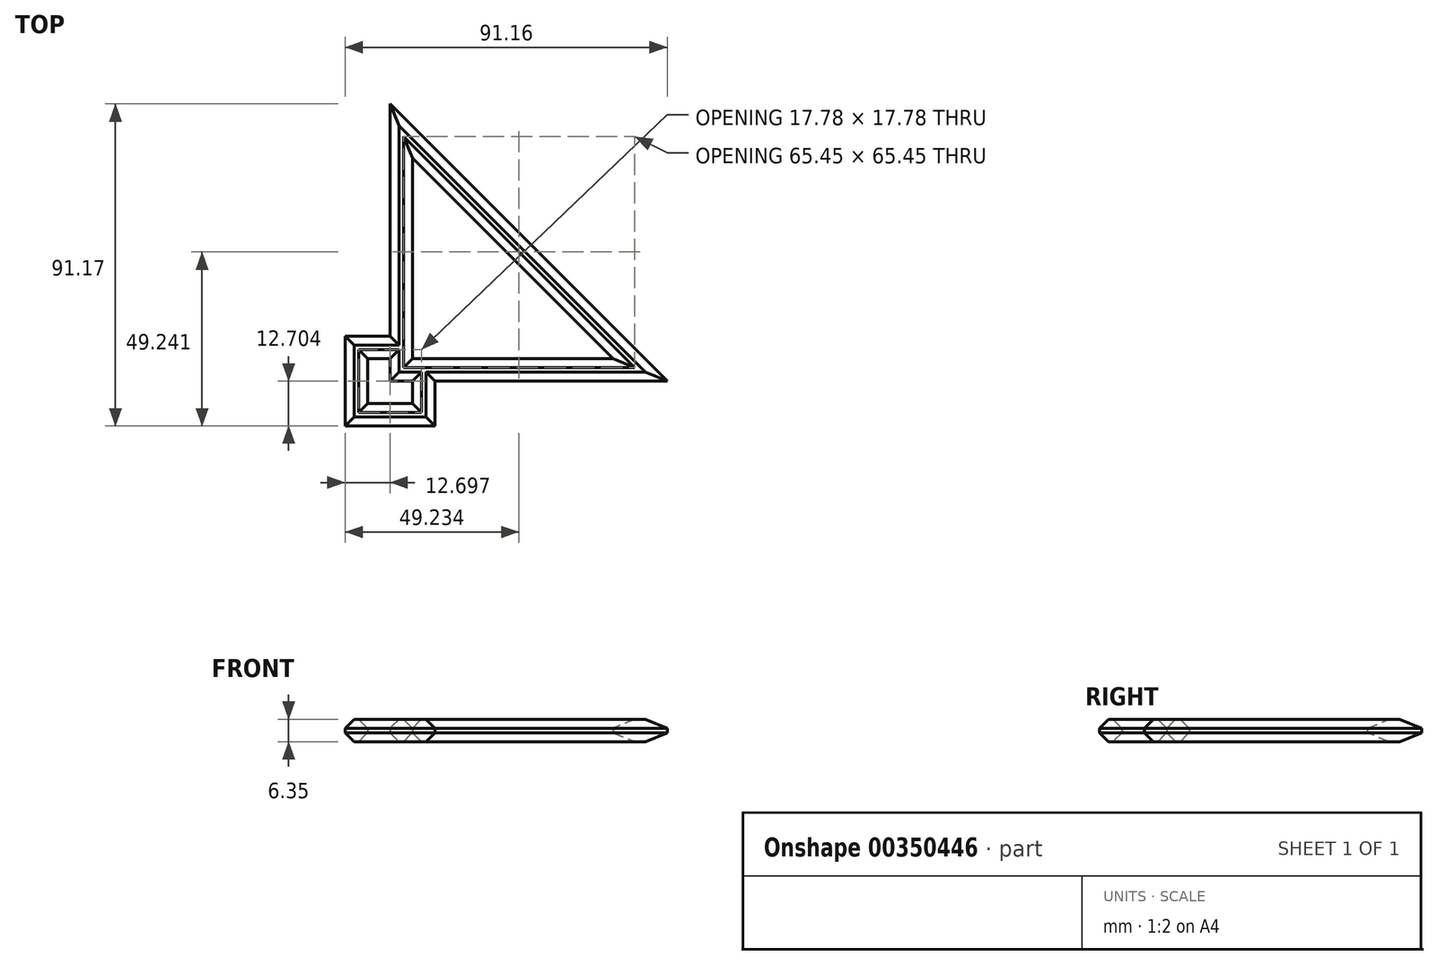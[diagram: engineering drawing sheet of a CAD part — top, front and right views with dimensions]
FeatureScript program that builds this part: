
annotation { "Feature Type Name" : "Feature", "Feature Type Description" : "" }
export const myFeature = defineFeature(function(context is Context, id is Id, definition is map)
    precondition{}
    {
        {
            var Q0;
            Q0=qCreatedBy(makeId("Top.planeOp"),FACE);
            var sketch = newSketch(context, id + "F0", { "sketchPlane" : qUnion([Q0])});
            skLineSegment(sketch, "E0", {"start": v(62.73, -3.4) * mm, "end": v(62.73, 2.94) * mm});
            skLineSegment(sketch, "E1", {"start": v(62.73, 2.94) * mm, "end": v(-3.03, 2.94) * mm});
            skLineSegment(sketch, "E2", {"start": v(-3.03, -0.37) * mm, "end": v(-3.03, 68.7) * mm});
            skLineSegment(sketch, "E3", {"start": v(-3.03, 68.7) * mm, "end": v(-9.38, 68.7) * mm});
            skLineSegment(sketch, "E4", {"start": v(-3.03, 68.7) * mm, "end": v(62.73, 2.94) * mm});
            skLineSegment(sketch, "E5", {"start": v(-3.03, 59.73) * mm, "end": v(53.75, 2.94) * mm});
            skLineSegment(sketch, "E6", {"start": v(-9.38, 68.7) * mm, "end": v(-9.38, 72.28) * mm});
            skLineSegment(sketch, "E7", {"start": v(-3.03, 68.7) * mm, "end": v(-9.38, 75.06) * mm});
            skLineSegment(sketch, "E8", {"start": v(62.73, 2.94) * mm, "end": v(69.08, -3.4) * mm});
            skLineSegment(sketch, "E9", {"start": v(-9.38, 72.28) * mm, "end": v(-9.38, 75.06) * mm});
            skLineSegment(sketch, "E10", {"start": v(-9.38, 9.3) * mm, "end": v(-22.08, 9.3) * mm});
            skLineSegment(sketch, "E11", {"start": v(-15.73, 2.94) * mm, "end": v(-15.73, -9.76) * mm});
            skLineSegment(sketch, "E12", {"start": v(-15.73, -9.76) * mm, "end": v(-3.03, -9.76) * mm});
            skLineSegment(sketch, "E13", {"start": v(-3.03, -9.76) * mm, "end": v(-3.03, -3.4) * mm});
            skLineSegment(sketch, "E14", {"start": v(-22.08, 9.3) * mm, "end": v(-22.08, -16.1) * mm});
            skLineSegment(sketch, "E15", {"start": v(-22.08, -16.1) * mm, "end": v(3.32, -16.1) * mm});
            skLineSegment(sketch, "E16", {"start": v(3.32, -16.1) * mm, "end": v(3.32, -3.4) * mm});
            skLineSegment(sketch, "E17", {"start": v(-9.38, 9.3) * mm, "end": v(-9.38, 68.7) * mm});
            skLineSegment(sketch, "E18", {"start": v(3.32, -3.4) * mm, "end": v(62.73, -3.4) * mm});
            skLineSegment(sketch, "E19", {"start": v(62.73, -3.4) * mm, "end": v(69.08, -3.4) * mm});
            skLineSegment(sketch, "E20", {"start": v(-3.03, 2.94) * mm, "end": v(-50.84, -44.86) * mm, "construction": true});
            skLineSegment(sketch, "E21", {"start": v(-3.03, -3.4) * mm, "end": v(-9.38, -3.4) * mm});
            skLineSegment(sketch, "E22", {"start": v(-9.38, -3.4) * mm, "end": v(-9.38, 2.94) * mm});
            skLineSegment(sketch, "E23", {"start": v(-9.38, 2.94) * mm, "end": v(-15.73, 2.94) * mm});
            skSolve(sketch);
        }
        {
            var Q0;
            {var subQ5=sQuery(id+"F0.wireOp",EDGE,"E0");Q0=makeQuery(id+"F0.imprint","IMPRINT",FACE,{"disambiguationData":[TD([[makeQuery(id+"F0.imprint","IMPRINT",EDGE,{"derivedFrom":subQ5}),1.0]])]});}
            var Q1;
            {var subQ0=sQuery(id+"F0.wireOp",EDGE,"E4");Q1=makeQuery(id+"F0.imprint","IMPRINT",FACE,{"disambiguationData":[TD([[makeQuery(id+"F0.imprint","IMPRINT",EDGE,{"derivedFrom":subQ0}),-1.0]])]});}
            var Q2;
            Q2=makeQuery(id+"F0.imprint","IMPRINT",FACE,{"disambiguationData":[TD([[makeQuery(id+"F0.imprint","IMPRINT",EDGE,{"derivedFrom":sQuery(id+"F0.wireOp",EDGE,"E3")}),-1.0]])]});
            var Q3;
            {var subQ0=sQuery(id+"F0.wireOp",EDGE,"E0");Q3=makeQuery(id+"F0.imprint","IMPRINT",FACE,{"disambiguationData":[TD([[makeQuery(id+"F0.imprint","IMPRINT",EDGE,{"derivedFrom":subQ0}),-1.0]])]});}
            extrude(context, id + "F1", {"entities" : qUnion([Q0, Q1, Q2, Q3]), "depth" : 6.35 * mm, "offsetDistance" : 25.4 * mm});
        }
        {
            var Q0;
            Q0=makeQuery(id+"F1.opExtrude","CAP_FACE",FACE,{"disambiguationData":[OSD([sQuery(id+"F0.wireOp",EDGE,"E1"),sQuery(id+"F0.wireOp",EDGE,"E2"),sQuery(id+"F0.wireOp",EDGE,"E4"),sQuery(id+"F0.wireOp",EDGE,"E5"),sQuery(id+"F0.wireOp",EDGE,"E6"),sQuery(id+"F0.wireOp",EDGE,"E7"),sQuery(id+"F0.wireOp",EDGE,"E8"),sQuery(id+"F0.wireOp",EDGE,"E9"),sQuery(id+"F0.wireOp",EDGE,"E10"),sQuery(id+"F0.wireOp",EDGE,"E11"),sQuery(id+"F0.wireOp",EDGE,"E12"),sQuery(id+"F0.wireOp",EDGE,"E13"),sQuery(id+"F0.wireOp",EDGE,"E14"),sQuery(id+"F0.wireOp",EDGE,"E15"),sQuery(id+"F0.wireOp",EDGE,"E16"),sQuery(id+"F0.wireOp",EDGE,"E17"),sQuery(id+"F0.wireOp",EDGE,"E18"),sQuery(id+"F0.wireOp",EDGE,"E19"),sQuery(id+"F0.wireOp",EDGE,"E21"),sQuery(id+"F0.wireOp",EDGE,"E22"),sQuery(id+"F0.wireOp",EDGE,"E23")])],"isStart":false});
            var Q1;
            Q1=makeQuery(id+"F1.opExtrude","CAP_FACE",FACE,{"disambiguationData":[OSD([sQuery(id+"F0.wireOp",EDGE,"E1"),sQuery(id+"F0.wireOp",EDGE,"E2"),sQuery(id+"F0.wireOp",EDGE,"E4"),sQuery(id+"F0.wireOp",EDGE,"E5"),sQuery(id+"F0.wireOp",EDGE,"E6"),sQuery(id+"F0.wireOp",EDGE,"E7"),sQuery(id+"F0.wireOp",EDGE,"E8"),sQuery(id+"F0.wireOp",EDGE,"E9"),sQuery(id+"F0.wireOp",EDGE,"E10"),sQuery(id+"F0.wireOp",EDGE,"E11"),sQuery(id+"F0.wireOp",EDGE,"E12"),sQuery(id+"F0.wireOp",EDGE,"E13"),sQuery(id+"F0.wireOp",EDGE,"E14"),sQuery(id+"F0.wireOp",EDGE,"E15"),sQuery(id+"F0.wireOp",EDGE,"E16"),sQuery(id+"F0.wireOp",EDGE,"E17"),sQuery(id+"F0.wireOp",EDGE,"E18"),sQuery(id+"F0.wireOp",EDGE,"E19"),sQuery(id+"F0.wireOp",EDGE,"E21"),sQuery(id+"F0.wireOp",EDGE,"E22"),sQuery(id+"F0.wireOp",EDGE,"E23")])],"isStart":true});
            chamfer(context, id + "F2", {"entities" : qUnion([Q0, Q1]), "width" : 2.54 * mm, "tangentPropagation" : true});
        }
    });
